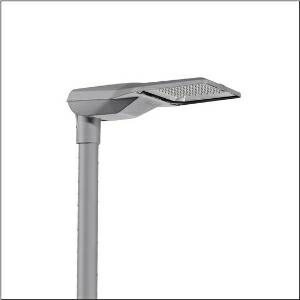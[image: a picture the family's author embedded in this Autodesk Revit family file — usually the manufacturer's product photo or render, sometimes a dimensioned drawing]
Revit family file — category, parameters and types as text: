
# Revit family: streetlight_sl_21_iq_midi___st0_8a_5xe3c41d08nb_52df
name_source: partatom
category: Lighting Fixtures
units: mm (PartAtom-declared; Revit-internal decimal feet)

## family parameters
Cut with Voids When Loaded = No
Host = Face
Light Source = No
Part Type = Normal
Room Calculation Point = No
Round Connector Dimension = Use Diameter
Shared = No

## types (1)
- --- (1 x LED, 24250 lm, 155.5 W, 4000K)
    Apparent Load = 155 VA
    CIE Flux Codes = 41 75 97 100 100
    Color Rendering = 70
    Color Temperature = 4000K
    Default Elevation = 1800 mm
    Description = Streetlight SL 21 iQ midi, mast luminaire, primary light control with lens, of PMMA, primary optical cover: cover, of toughened safety glass, transparent, light distribution: ST0.8a, light emission: direct distribution, primary light characteristic: asymmetric, installation type: post-top, side-entry, LED, High Power LED, rated luminous flux: 24.250lm, luminous efficacy: 156lm/W, light colour: 740, colour temperature: 4000K, control gear: iQ-Comfort, control: Auto-Match, Temp-Guard, Lumen-Switch, Night-Set, Smart-Wire, Light-Fading, Desk-Remote (wireless, voltage-free reading and setting of iQ features in the workshop via application-optimized NFC function/RFID function), optimised constant luminous flux control (CLO 2.0), pre-setting: linear dimming characteristic, mains connection: 230..240V, AC, 50/60Hz, start of lifetime: 156W, end of service life: 162W, reduction: 69W, luminaire housing, of diecast aluminium, powder-coated, SITECO metallic grey (DB 702S), corrosivity category C5 high according to DIN EN ISO 12944, please order mast flange separately, inclination adjustable: 0°, 5°, 10°, 15°, sealing non-destructively replaceable, multi-level sealing system, length: 644mm, width: 335mm, height: 110mm, mast flange for spigot size: 42mm (side-entry): 5XC10008XM4, 60/48mm (side-entry/post-top): 5XC10108XM2, 76/60mm (side-entry/post-top): 5XC10108XM1, mounting height: 4..8m, protection rating (complete): IP66, insulation class (complete): insulation class II (safety insulation), certification: CE, ENEC, ENEC+, VDE, impact resistance: IK10, permissible operating ambient temperature for outdoor applications: -40..+50°C, standard-compliant lighting for roads and squares, packaging unit: 1 piece

Light Distribution: ST0.8a
    Height = 111 mm
    Lamp = 1 x LED
    Lamp Light Flux = 24250 lm
    Lamp Power = 155.5 W
    Lamp count = 1
    Length = 644 mm
    Luminous efficacy = 156 lm/W
    Manufacturer = Siteco
    ModVariant = No
    Model = 5XE3C41D08NB
    Number of Poles = 1
    OnlyDefault = Yes
    Power Factor = 1
    Product Name = Streetlight SL 21 iQ midi | ST0.8a
    Product group = mast luminaire | pylon top
    ProductGroupID = 6100
    Protection Class = Protection class II
    Protection Degree = IP 66
    RLX_Detail_Level = 1
    RLX_Emergency_Light_Flux = 0 lm
    RLX_Emergency_Type = 0
    RLX_Emergency_Type_DB = No
    RlxData = <blob elided: 27217 chars, md5=62f3e542>
    Socket = socket
    Standby Power = 0 W
    System Light Flux = 24250 lm
    System Power = 155 W
    Type Comments = factory setting: luminous flux: 100 % | dim-lin: 254 | 823 mA
    Type Image = l_1004298.jpg
    URL = http://relux.com
    VarID = @adj_168393
    Voltage = 0 V
    Weight = 0.00 kg
    Width = 336 mm

## geometry (parser evidence)
native form markers: Blend x4, Sweep x12
no freeform markers — native parametric forms only
